# Revit family: 318_312f0b91a3a245878bb449fb9afdf0
name_source: partatom
category: Pipe Accessories
units: mm (PartAtom-declared; Revit-internal decimal feet)

## family parameters
Always vertical = Yes
Cut with Voids When Loaded = No
Part Type = Valve - Normal
Round Connector Dimension = Use Diameter
Shared = No
Work Plane-Based = No

## types (1)
- FAR-3874 21100
    BP = 25 mm
    CAT0 = Yes
    CenSd_R3_6 = 28 mm
    D = 27 mm  [stored 0.0885827 ft]
    Description = START 2" flanged joint manifold f-f, 1 port 1" f, 100 mm
    E = 35 mm  [stored 0.114829 ft]
    H1 = 47 mm  [stored 0.154199 ft]
    H2 = 33 mm
    L1 = 49 mm  [stored 0.160761 ft]
    L2 = 51 mm
    L3 = 10 mm  [stored 0.0328084 ft]
    L3__ve = -10 mm  [stored -0.0328084 ft]
    L4 = 29 mm
    L4__ve = -29 mm  [stored -0.0951444 ft]
    L5 = 31 mm  [stored 0.101706 ft]
    MP1 = 50 mm
    MP2 = 50 mm
    Manufacturer = FAR
    QmdConnectorList = 301;MP1;302;MP2;303;BP
    R1 = 25 mm  [stored 0.082021 ft]
    R3 = 33 mm
    R4 = 28 mm
    R5 = 19 mm
    R6 = 22 mm
    R8 = 15 mm  [stored 0.0492126 ft]
    URL = www.far.eu
    W1 = 12 mm  [stored 0.0393701 ft]
    W3 = 51 mm
    W3__ve = -51 mm
    W4 = 5 mm  [stored 0.0164042 ft]
    W4__ve = -5 mm
    W5 = 14 mm  [stored 0.0459318 ft]
    W5__ve = -14 mm
    magiPartTypeId = 318
    magiProductCode = FAR-3874 21100
    magiProductFamilyId = 312f0b91a3a245878bb449fb9afdf0
    magiProductId = 312f0b91a3a245878bb449fb9afdf0

note: [stored X ft] marks values corroborated as IEEE doubles in the binary element streams (Revit-internal decimal feet)

## geometry (parser evidence)
native form markers: Sweep x2
no freeform markers — native parametric forms only
